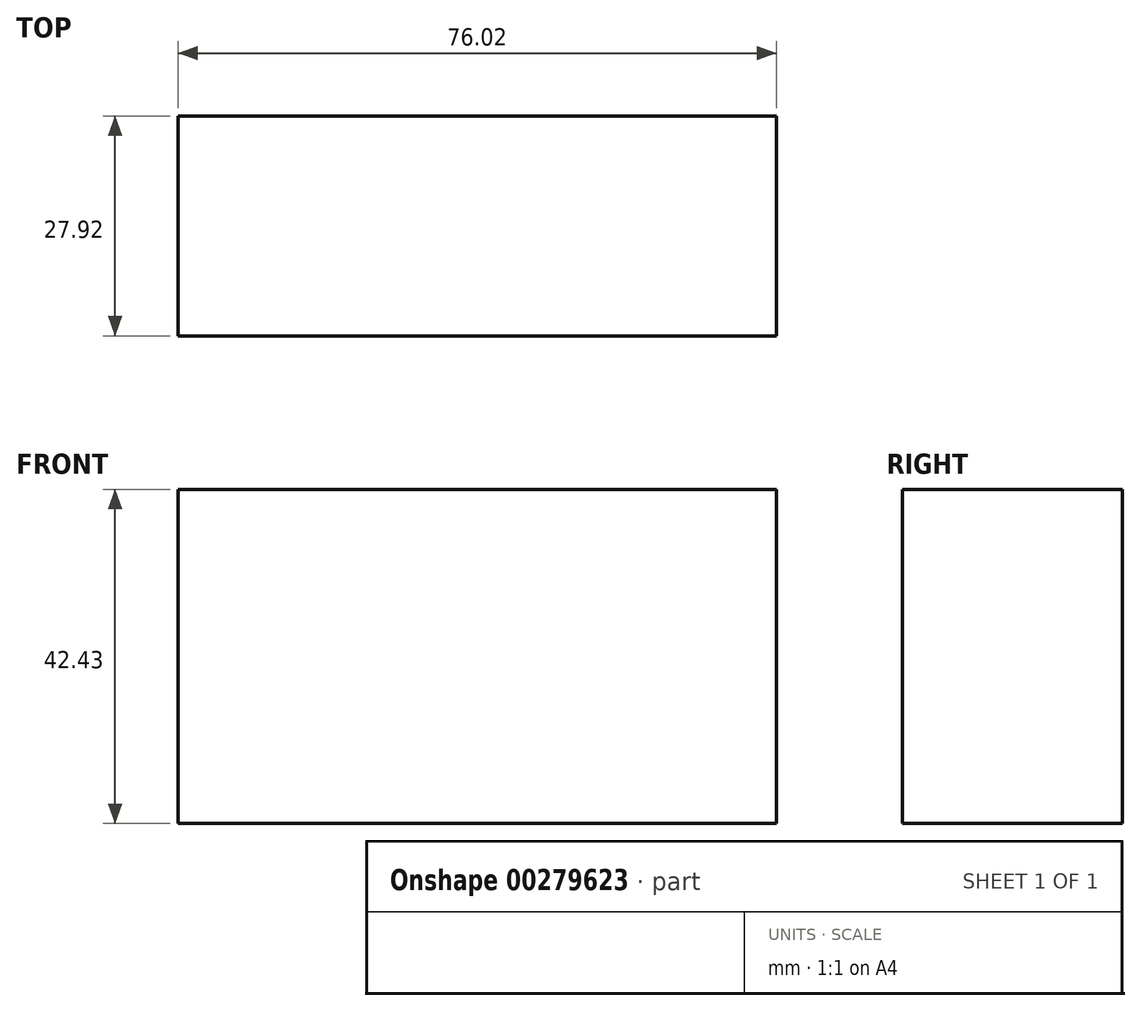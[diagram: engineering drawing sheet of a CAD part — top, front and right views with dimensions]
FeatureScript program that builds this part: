
annotation { "Feature Type Name" : "Feature", "Feature Type Description" : "" }
export const myFeature = defineFeature(function(context is Context, id is Id, definition is map)
    precondition{}
    {
        {
            var Q0;
            Q0=qCreatedBy(makeId("Front.planeOp"),FACE);
            var sketch = newSketch(context, id + "F0", { "sketchPlane" : qUnion([Q0])});
            skLineSegment(sketch, "E0.bottom", {"start": v(0, 0) * mm, "end": v(76.02, 0) * mm});
            skLineSegment(sketch, "E0.top", {"start": v(0, 42.43) * mm, "end": v(76.02, 42.43) * mm});
            skLineSegment(sketch, "E0.left", {"start": v(0, 0) * mm, "end": v(0, 42.43) * mm});
            skLineSegment(sketch, "E0.right", {"start": v(76.02, 0) * mm, "end": v(76.02, 42.43) * mm});
            skLineSegment(sketch, "E1.bottom", {"start": v(-21.8, 103.72) * mm, "end": v(-28.44, 103.72) * mm});
            skLineSegment(sketch, "E1.top", {"start": v(-21.8, 108.73) * mm, "end": v(-28.44, 108.73) * mm});
            skLineSegment(sketch, "E1.left", {"start": v(-21.8, 103.72) * mm, "end": v(-21.8, 108.73) * mm});
            skLineSegment(sketch, "E1.right", {"start": v(-28.44, 103.72) * mm, "end": v(-28.44, 108.73) * mm});
            skSolve(sketch);
        }
        {
            var Q0;
            Q0=makeQuery(id+"F0.imprint","IMPRINT",FACE,{"disambiguationData":[TD([[makeQuery(id+"F0.imprint","IMPRINT",EDGE,{"derivedFrom":sQuery(id+"F0.wireOp",EDGE,"E0.bottom")}),1.0]])]});
            extrude(context, id + "F1", {"entities" : qUnion([Q0]), "depth" : 27.92 * mm});
        }
    });
